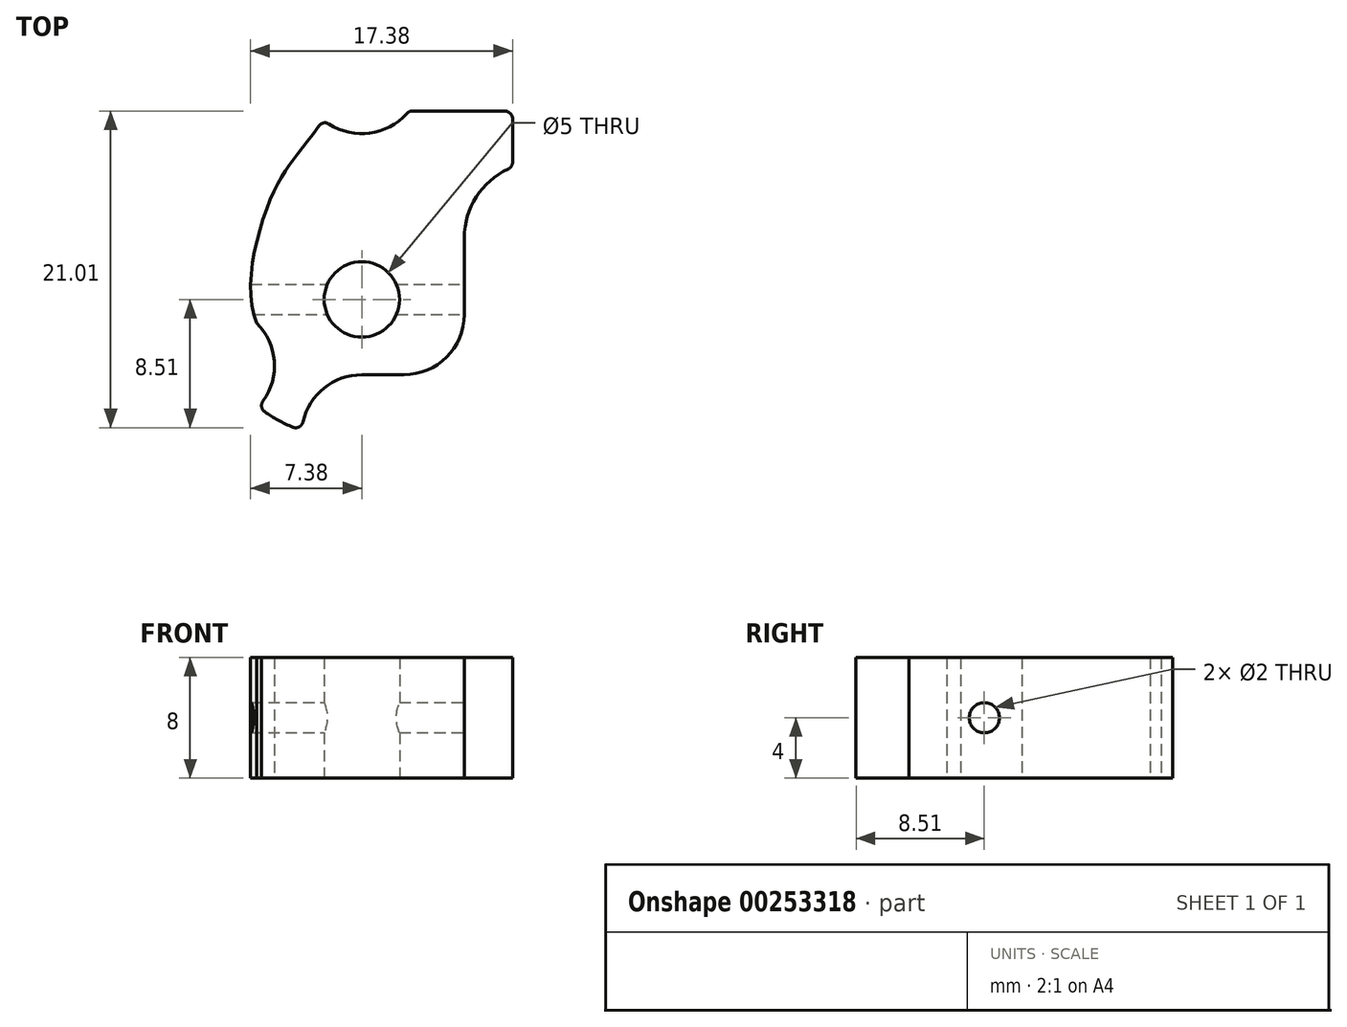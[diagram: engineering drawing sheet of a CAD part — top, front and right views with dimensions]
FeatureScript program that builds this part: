
annotation { "Feature Type Name" : "Feature", "Feature Type Description" : "" }
export const myFeature = defineFeature(function(context is Context, id is Id, definition is map)
    precondition{}
    {
        {
            var Q0;
            Q0=qCreatedBy(makeId("Top.planeOp"),FACE);
            var sketch = newSketch(context, id + "F0", { "sketchPlane" : qUnion([Q0])});
            skCircle(sketch, "E0", {"center": v(0, 0) * mm, "radius": 2.5 * mm});
            skArc(sketch, "E1", {"start": v(0, -5) * mm, "mid": v(-2.72, -6.06) * mm, "end": v(-3.99, -8.69) * mm});
            skArc(sketch, "E2", {"start": v(2.8, -5) * mm, "mid": v(5.63, -3.83) * mm, "end": v(6.8, -1) * mm});
            skArc(sketch, "E3", {"start": v(-2.56, 11.93) * mm, "mid": v(0.4, 11.02) * mm, "end": v(3.12, 12.5) * mm});
            skLineSegment(sketch, "E4", {"start": v(0, -5) * mm, "end": v(2.8, -5) * mm});
            skLineSegment(sketch, "E5", {"start": v(6.8, -1) * mm, "end": v(6.8, 4.1) * mm});
            skLineSegment(sketch, "E6", {"start": v(10, 12.5) * mm, "end": v(10, 8.77) * mm});
            skLineSegment(sketch, "E7", {"start": v(10, 12.5) * mm, "end": v(3.12, 12.5) * mm});
            skArc(sketch, "E8", {"start": v(10, 8.77) * mm, "mid": v(7.68, 6.94) * mm, "end": v(6.8, 4.1) * mm});
            skArc(sketch, "E9", {"start": v(-6.86, -7.12) * mm, "mid": v(-5.5, -8.04) * mm, "end": v(-3.99, -8.69) * mm});
            skFitSpline(sketch, "E10", {"points": [v(-6.97, -1.57) * mm, v(-5.79, 7.28) * mm, v(-2.56, 11.93) * mm], "startDerivative": vector(-5.61, 12.56) * mm, "endDerivative": vector(10.2, 14.9) * mm});
            skArc(sketch, "E11", {"start": v(-6.86, -7.12) * mm, "mid": v(-5.8, -4.32) * mm, "end": v(-6.97, -1.57) * mm});
            skSolve(sketch);
        }
        {
            var Q0;
            Q0=makeQuery(id+"F0.imprint","IMPRINT",FACE,{"disambiguationData":[TD([[makeQuery(id+"F0.imprint","IMPRINT",EDGE,{"derivedFrom":sQuery(id+"F0.wireOp",EDGE,"E0")}),-1.0]])]});
            extrude(context, id + "F1", {"entities" : qUnion([Q0]), "depth" : 8 * mm});
        }
        {
            var Q0;
            Q0=makeQuery(id+"F1.opExtrude","SWEPT_EDGE",EDGE,{"disambiguationData":[OSD([sQuery(id+"F0.wireOp",EDGE,"E6"),sQuery(id+"F0.wireOp",EDGE,"E7")])]});
            var Q1;
            Q1=makeQuery(id+"F1.opExtrude","SWEPT_EDGE",EDGE,{"disambiguationData":[OSD([sQuery(id+"F0.wireOp",EDGE,"E3"),sQuery(id+"F0.wireOp",EDGE,"E7")])]});
            var Q2;
            Q2=makeQuery(id+"F1.opExtrude","SWEPT_EDGE",EDGE,{"disambiguationData":[OSD([sQuery(id+"F0.wireOp",EDGE,"E3"),sQuery(id+"F0.wireOp",EDGE,"E10")])]});
            var Q3;
            Q3=makeQuery(id+"F1.opExtrude","SWEPT_EDGE",EDGE,{"disambiguationData":[OSD([sQuery(id+"F0.wireOp",EDGE,"E6"),sQuery(id+"F0.wireOp",EDGE,"E8")])]});
            var Q4;
            Q4=makeQuery(id+"F1.opExtrude","SWEPT_EDGE",EDGE,{"disambiguationData":[OSD([sQuery(id+"F0.wireOp",EDGE,"E1"),sQuery(id+"F0.wireOp",EDGE,"E9")])]});
            var Q5;
            Q5=makeQuery(id+"F1.opExtrude","SWEPT_EDGE",EDGE,{"disambiguationData":[OSD([sQuery(id+"F0.wireOp",EDGE,"E9"),sQuery(id+"F0.wireOp",EDGE,"E11")])]});
            fillet(context, id + "F2", {"entities" : qUnion([Q0, Q1, Q2, Q3, Q4, Q5]), "radius" : .5 * mm, "allowEdgeOverflow" : false});
        }
        {
            var Q0;
            Q0=qCreatedBy(makeId("Right.planeOp"),FACE);
            var sketch = newSketch(context, id + "F3", { "sketchPlane" : qUnion([Q0])});
            skCircle(sketch, "E12", {"center": v(0, 4) * mm, "radius": 1 * mm});
            skPoint(sketch, "E13.0", {"position": v(0, 0) * mm});
            skLineSegment(sketch, "E14", {"start": v(2.5, 8) * mm, "end": v(2.5, 0) * mm, "construction": true});
            skLineSegment(sketch, "E15", {"start": v(-2.5, 0) * mm, "end": v(-2.5, 8) * mm, "construction": true});
            skLineSegment(sketch, "E16", {"start": v(0, 0) * mm, "end": v(0, 12.46) * mm, "construction": true});
            skSolve(sketch);
        }
        {
            var Q0;
            Q0 = qSketchRegion(id + "F3", true);
            extrude(context, id + "F4", {"entities" : qUnion([Q0]), "operationType" : NewBodyOperationType.REMOVE, "endBound" : BoundingType.SYMMETRIC, "oppositeDirection" : true, "depth" : 25 * mm});
        }
    });
